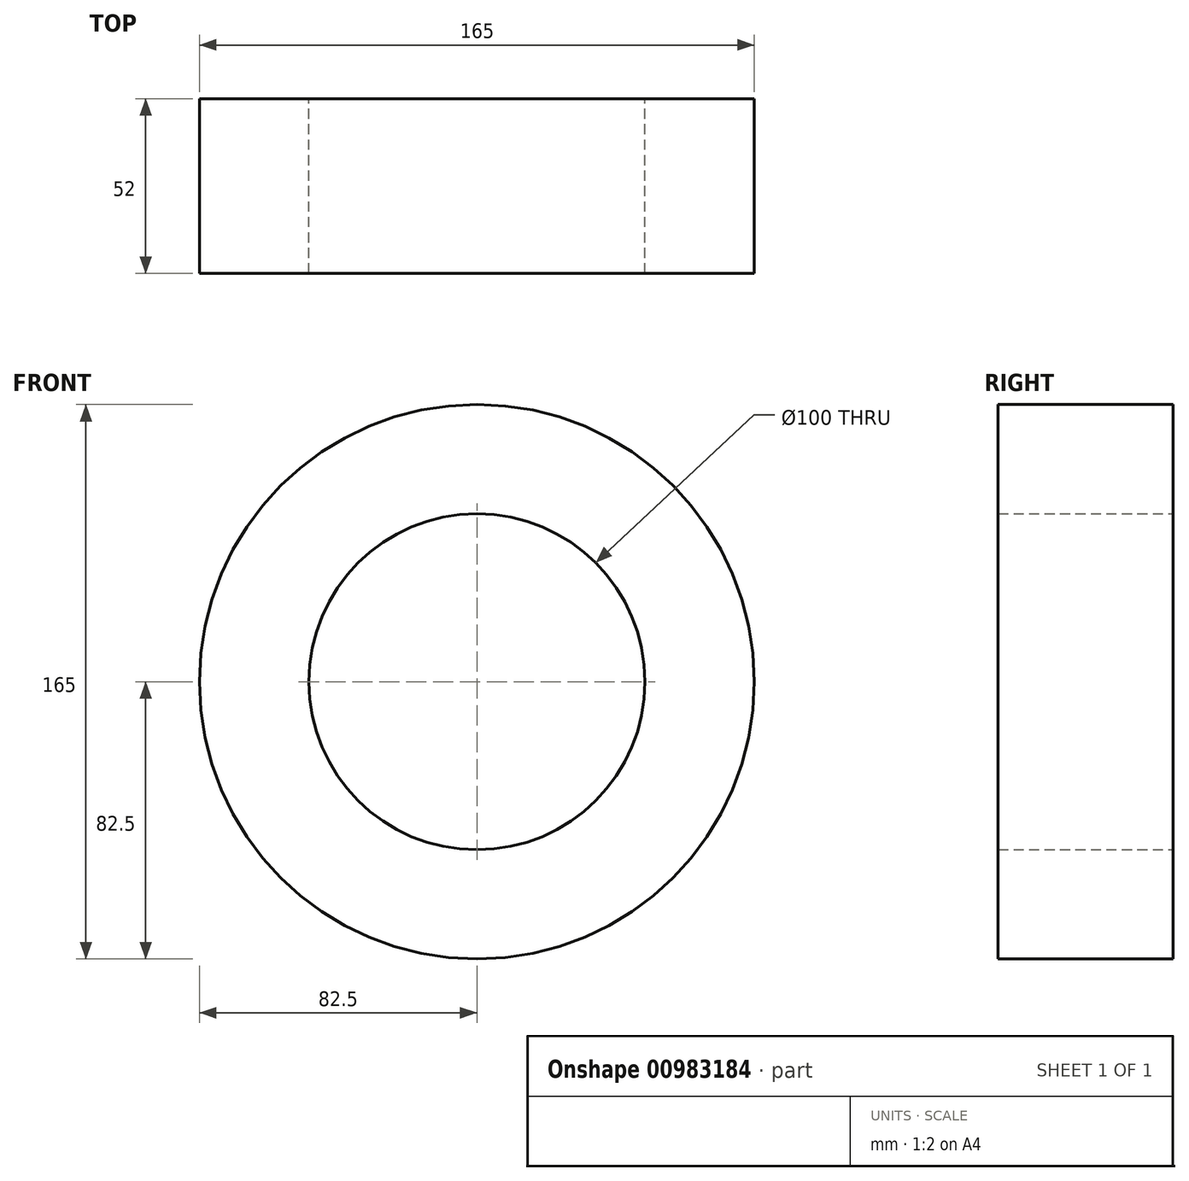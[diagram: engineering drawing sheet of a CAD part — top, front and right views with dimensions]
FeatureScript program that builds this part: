
annotation { "Feature Type Name" : "Feature", "Feature Type Description" : "" }
export const myFeature = defineFeature(function(context is Context, id is Id, definition is map)
    precondition{}
    {
        {
            var Q0;
            Q0=qCreatedBy(makeId("Front.planeOp"),FACE);
            var sketch = newSketch(context, id + "F0", { "sketchPlane" : qUnion([Q0])});
            skCircle(sketch, "E0", {"center": v(0, 0) * mm, "radius": 82.5 * mm});
            skCircle(sketch, "E1", {"center": v(0, 0) * mm, "radius": 50 * mm});
            skSolve(sketch);
        }
        {
            var Q0;
            Q0=makeQuery(id+"F0.imprint","IMPRINT",FACE,{"disambiguationData":[TD([[makeQuery(id+"F0.imprint","IMPRINT",EDGE,{"derivedFrom":sQuery(id+"F0.wireOp",EDGE,"E0")}),1.0]])]});
            extrude(context, id + "F1", {"entities" : qUnion([Q0]), "depth" : 52 * mm, "offsetDistance" : 25 * mm});
        }
    });
